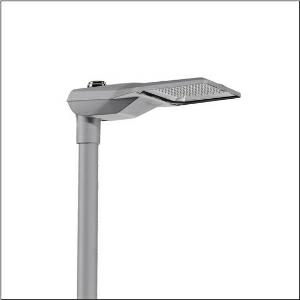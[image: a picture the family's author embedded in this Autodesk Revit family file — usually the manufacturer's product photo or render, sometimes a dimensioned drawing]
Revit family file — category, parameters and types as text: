
# Revit family: streetlight_sl_21_midi___st1_0a_5xe7d57n08nb_4101
name_source: partatom
category: Lighting Fixtures
units: mm (PartAtom-declared; Revit-internal decimal feet)

## family parameters
Cut with Voids When Loaded = No
Host = Face
Light Source = No
Part Type = Normal
Room Calculation Point = No
Round Connector Dimension = Use Diameter
Shared = No

## types (1)
- --- (1 x LED, 19520 lm, 151.2 W, 3000K)
    Apparent Load = 151 VA
    CIE Flux Codes = 40 73 97 100 100
    Color Rendering = 80
    Color Temperature = 3000K
    Default Elevation = 1800 mm
    Description = Streetlight SL 21 midi, mast luminaire, primary light control with lens, of PMMA, primary optical cover: cover, of toughened safety glass, transparent, light distribution: ST1.0a, light emission: direct distribution, primary light characteristic: asymmetric, installation type: side-entry, LED, 3G 2.5mm², High Power LED, rated luminous flux: 19.520lm, luminous efficacy: 129lm/W, light colour: 830, colour temperature: 3000K, control gear: NEMA (7pin), control: overheat protection, pre-setting: linear dimming characteristic, constant luminous flux control, time-dependent luminous flux control, flexible luminous flux parameterisation, mains connection: 220..240V, AC, 50/60Hz, connection cable pre-assembled, cable length: 12,5m, wiring characteristics: H05VV-F, start of lifetime: 151W, end of service life: 157W, reduction: 70W, luminaire housing, of diecast aluminium (EN AC-44300), powder-coated, SITECO metallic grey (DB 702S), corrosivity category C5 high according to DIN EN ISO 12944, multi-level sealing system, sealing non-destructively replaceable, inclination adjustable: 0°, 5°, 10°, 15°, length: 644mm, width: 335mm, height: 110mm, spigot size: 42mm (side-entry), mounting height: 4..8m, protection rating (complete): IP66, insulation class (complete): insulation class I (protective earthing), certification: CE, ENEC, ENEC+, VDE, impact resistance: IK10, permissible operating ambient temperature for outdoor applications: -40..+50°C, standard-compliant lighting for roads and squares, packaging unit: 1 piece

Light Distribution: ST1.0a
    Height = 111 mm
    Lamp = 1 x LED
    Lamp Light Flux = 19520 lm
    Lamp Power = 151.2 W
    Lamp count = 1
    Length = 644 mm
    Luminous efficacy = 129 lm/W
    Manufacturer = Siteco
    ModVariant = No
    Model = 5XE7D57N08NB
    Number of Poles = 1
    OnlyDefault = Yes
    Power Factor = 1
    Product Name = Streetlight SL 21 midi | ST1.0a
    Product group = mast luminaire | pylon top
    ProductGroupID = 6100
    Protection Class = Protection class I
    Protection Degree = IP 66
    RLX_Detail_Level = 1
    RLX_Emergency_Light_Flux = 0 lm
    RLX_Emergency_Type = 0
    RLX_Emergency_Type_DB = No
    RlxData = <blob elided: 26669 chars, md5=28d01338>
    Socket = socket
    Standby Power = 0 W
    System Light Flux = 19520 lm
    System Power = 151 W
    Type Comments = factory setting: luminous flux: 100 % | dim-lin: 254 | 802 mA
    Type Image = l_1294377.jpg
    URL = http://relux.com
    VarID = @adj_134585
    Voltage = 0 V
    Weight = 0.00 kg
    Width = 336 mm

## geometry (parser evidence)
native form markers: Blend x4, Sweep x11
no freeform markers — native parametric forms only
